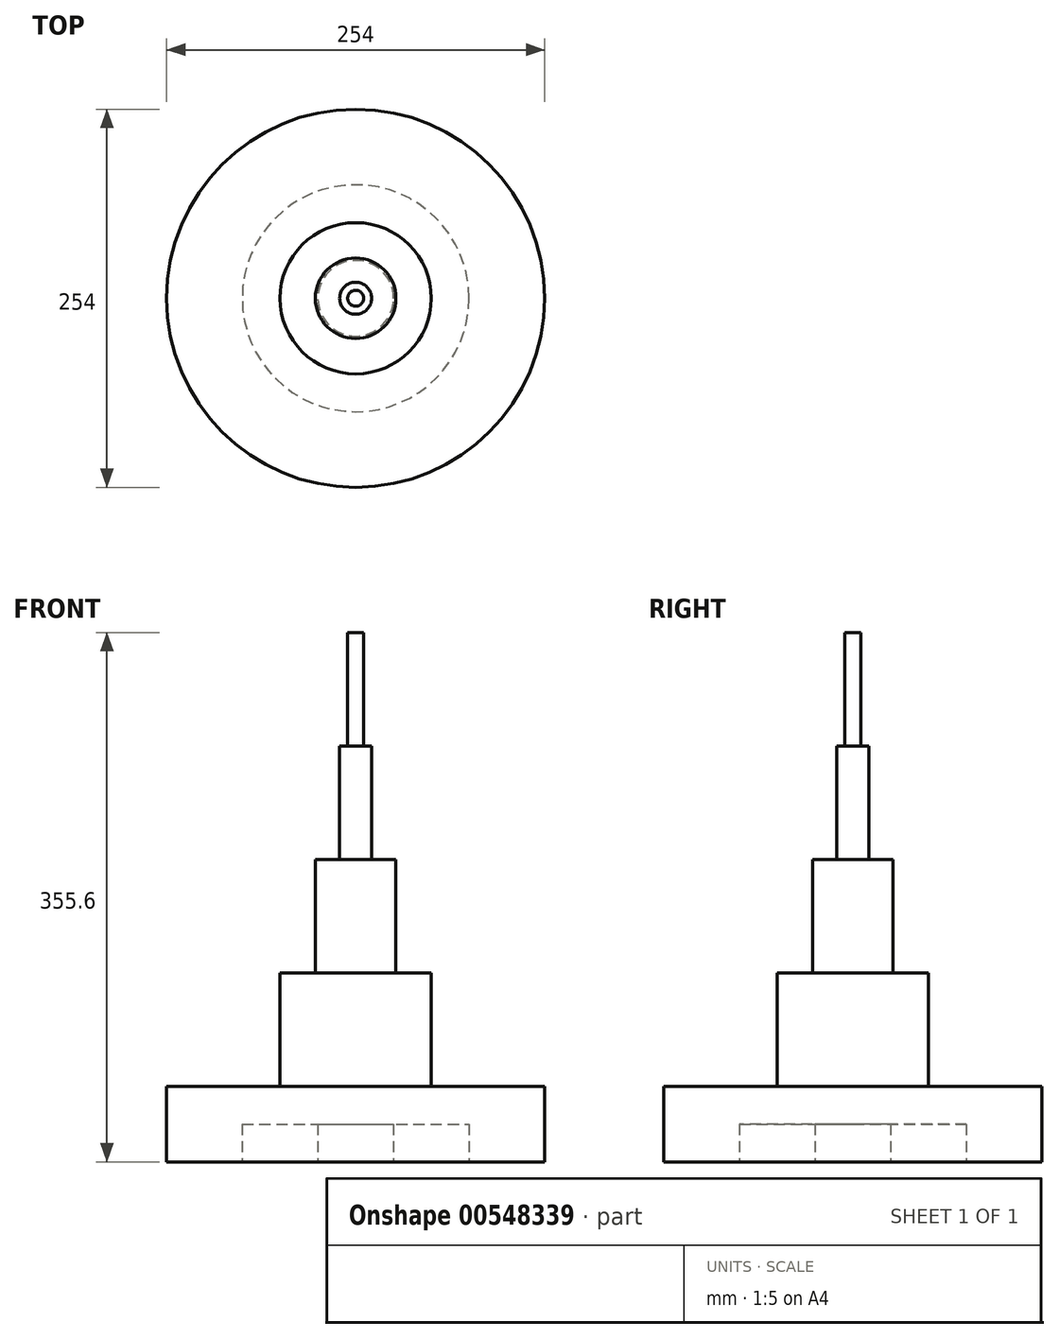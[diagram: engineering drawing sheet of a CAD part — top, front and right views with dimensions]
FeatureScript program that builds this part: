
annotation { "Feature Type Name" : "Feature", "Feature Type Description" : "" }
export const myFeature = defineFeature(function(context is Context, id is Id, definition is map)
    precondition{}
    {
        {
            var Q0;
            Q0=qCreatedBy(makeId("Front.planeOp"),FACE);
            var sketch = newSketch(context, id + "F0", { "sketchPlane" : qUnion([Q0])});
            skLineSegment(sketch, "E0", {"start": v(-67.63, -9.42) * mm, "end": v(-67.63, -60.22) * mm});
            skLineSegment(sketch, "E1", {"start": v(-67.63, -60.22) * mm, "end": v(-16.83, -60.22) * mm});
            skLineSegment(sketch, "E2", {"start": v(-16.83, -60.22) * mm, "end": v(-16.83, -34.82) * mm});
            skLineSegment(sketch, "E3", {"start": v(-16.83, -34.82) * mm, "end": v(33.97, -34.82) * mm});
            skLineSegment(sketch, "E4", {"start": v(33.97, -34.82) * mm, "end": v(33.97, -60.22) * mm});
            skLineSegment(sketch, "E5", {"start": v(33.97, -60.22) * mm, "end": v(59.37, -60.22) * mm});
            skLineSegment(sketch, "E6", {"start": v(59.37, -60.22) * mm, "end": v(59.37, 66.78) * mm});
            skLineSegment(sketch, "E7", {"start": v(59.37, 66.78) * mm, "end": v(8.57, 66.78) * mm});
            skLineSegment(sketch, "E8", {"start": v(8.57, 66.78) * mm, "end": v(8.57, -9.42) * mm});
            skLineSegment(sketch, "E9", {"start": v(8.57, -9.42) * mm, "end": v(-67.63, -9.42) * mm});
            skSolve(sketch);
        }
        {
            var Q0;
            Q0=makeQuery(id+"F0.imprint","IMPRINT",FACE,{"disambiguationData":[TD([[makeQuery(id+"F0.imprint","IMPRINT",EDGE,{"derivedFrom":sQuery(id+"F0.wireOp",EDGE,"E0")}),1.0]])]});
            var Q1;
            Q1=sQuery(id+"F0.wireOp",EDGE,"E6");
            revolve(context, id + "F1", {"entities" : qUnion([Q0]), "axis" : qUnion([Q1]), "revolveType" : RevolveType.FULL});
        }
        {
            var Q0;
            Q0=makeQuery(id+"F1.opRevolve","SWEPT_FACE",FACE,{"disambiguationData":[OSD([sQuery(id+"F0.wireOp",EDGE,"E7")])]});
            var sketch = newSketch(context, id + "F2", { "sketchPlane" : qUnion([Q0])});
            skCircle(sketch, "E10", {"center": v(59.37, 0) * mm, "radius": 27.05 * mm});
            skSolve(sketch);
        }
        {
            var Q0;
            Q0=makeQuery(id+"F2.imprint","IMPRINT",FACE,{"disambiguationData":[TD([[makeQuery(id+"F2.imprint","IMPRINT",EDGE,{"derivedFrom":sQuery(id+"F2.wireOp",EDGE,"E10")}),1.0]])]});
            extrude(context, id + "F3", {"entities" : qUnion([Q0]), "operationType" : NewBodyOperationType.ADD, "depth" : 76.2 * mm, "offsetDistance" : 25.4 * mm});
        }
        {
            var Q0;
            Q0=makeQuery(id+"F3.opExtrude","CAP_FACE",FACE,{"disambiguationData":[OSD([sQuery(id+"F2.wireOp",EDGE,"E10")])],"isStart":false});
            var sketch = newSketch(context, id + "F4", { "sketchPlane" : qUnion([Q0])});
            skCircle(sketch, "E11", {"center": v(59.37, 0) * mm, "radius": 10.77 * mm});
            skSolve(sketch);
        }
        {
            var Q0;
            Q0=makeQuery(id+"F4.imprint","IMPRINT",FACE,{"disambiguationData":[TD([[makeQuery(id+"F4.imprint","IMPRINT",EDGE,{"derivedFrom":sQuery(id+"F4.wireOp",EDGE,"E11")}),1.0]])]});
            extrude(context, id + "F5", {"entities" : qUnion([Q0]), "operationType" : NewBodyOperationType.ADD, "depth" : 76.2 * mm, "offsetDistance" : 25.4 * mm});
        }
        {
            var Q0;
            Q0=makeQuery(id+"F5.opExtrude","CAP_FACE",FACE,{"disambiguationData":[OSD([sQuery(id+"F4.wireOp",EDGE,"E11")])],"isStart":false});
            var sketch = newSketch(context, id + "F6", { "sketchPlane" : qUnion([Q0])});
            skCircle(sketch, "E12", {"center": v(59.37, 0) * mm, "radius": 5.38 * mm});
            skSolve(sketch);
        }
        {
            var Q0;
            Q0=makeQuery(id+"F6.imprint","IMPRINT",FACE,{"disambiguationData":[TD([[makeQuery(id+"F6.imprint","IMPRINT",EDGE,{"derivedFrom":sQuery(id+"F6.wireOp",EDGE,"E12")}),1.0]])]});
            extrude(context, id + "F7", {"entities" : qUnion([Q0]), "operationType" : NewBodyOperationType.ADD, "depth" : 76.2 * mm, "offsetDistance" : 25.4 * mm});
        }
    });
